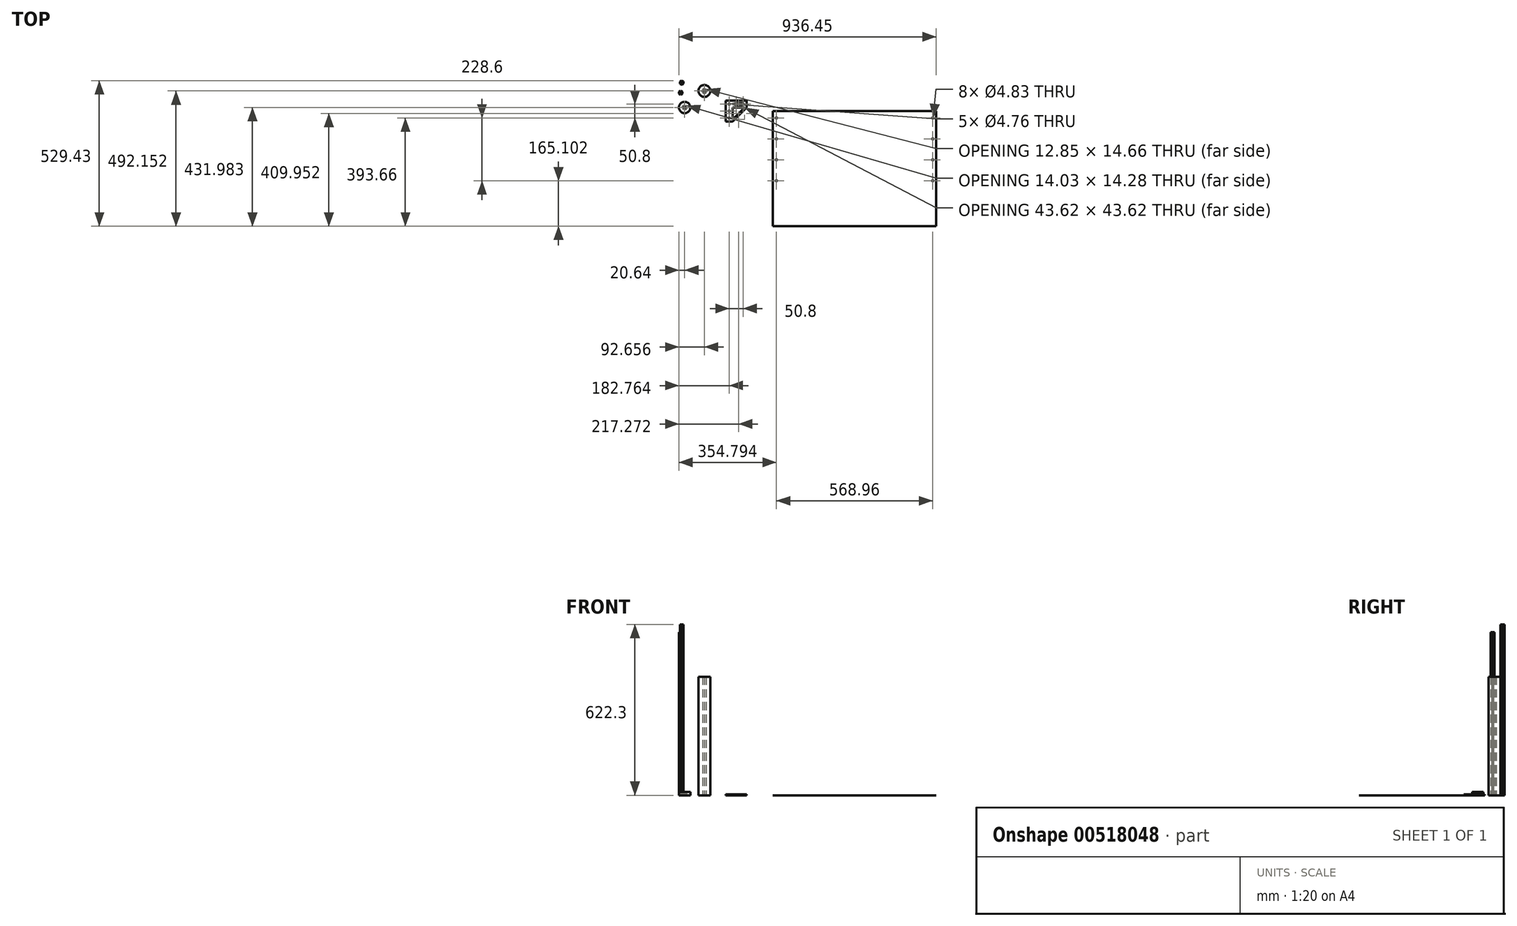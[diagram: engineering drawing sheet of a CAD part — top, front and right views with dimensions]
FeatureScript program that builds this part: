
annotation { "Feature Type Name" : "Feature", "Feature Type Description" : "" }
export const myFeature = defineFeature(function(context is Context, id is Id, definition is map)
    precondition{}
    {
        {
            var Q0;
            Q0=qCreatedBy(makeId("Top.planeOp"),FACE);
            var sketch = newSketch(context, id + "F0", { "sketchPlane" : qUnion([Q0])});
            skCircle(sketch, "E0.cCircle", {"center": v(-59.4, 64.97) * mm, "radius": 6.35 * mm, "construction": true});
            skLineSegment(sketch, "E0.0", {"start": v(-52.73, 61.92) * mm, "end": v(-58.7, 57.67) * mm});
            skLineSegment(sketch, "E0.1", {"start": v(-58.7, 57.67) * mm, "end": v(-65.37, 60.72) * mm});
            skLineSegment(sketch, "E0.2", {"start": v(-65.37, 60.72) * mm, "end": v(-66.07, 68.02) * mm});
            skLineSegment(sketch, "E0.3", {"start": v(-66.07, 68.02) * mm, "end": v(-60.1, 72.27) * mm});
            skLineSegment(sketch, "E0.4", {"start": v(-60.1, 72.27) * mm, "end": v(-53.42, 69.22) * mm});
            skLineSegment(sketch, "E0.5", {"start": v(-53.42, 69.22) * mm, "end": v(-52.73, 61.92) * mm});
            skPoint(sketch, "E0.0.midPoint", {"position": v(-55.71, 59.8) * mm});
            skCircle(sketch, "E1", {"center": v(-59.4, 64.97) * mm, "radius": 2.55 * mm});
            skSolve(sketch);
        }
        {
            var Q0;
            Q0=qSketchRegion(id+"F0",true);
            extrude(context, id + "F1", {"entities" : qUnion([Q0]), "depth" : 622.3 * mm});
        }
        {
            var Q0;
            Q0=qCreatedBy(makeId("Top.planeOp"),FACE);
            var sketch = newSketch(context, id + "F2", { "sketchPlane" : qUnion([Q0])});
            skCircle(sketch, "E2", {"center": v(23.03, 35) * mm, "radius": 21.59 * mm});
            skCircle(sketch, "E3.cCircle", {"center": v(23.03, 35) * mm, "radius": 6.35 * mm, "construction": true});
            skLineSegment(sketch, "E3.0", {"start": v(29.45, 31.46) * mm, "end": v(23.18, 27.66) * mm});
            skLineSegment(sketch, "E3.1", {"start": v(23.18, 27.66) * mm, "end": v(16.76, 31.2) * mm});
            skLineSegment(sketch, "E3.2", {"start": v(16.76, 31.2) * mm, "end": v(16.6, 38.52) * mm});
            skLineSegment(sketch, "E3.3", {"start": v(16.6, 38.52) * mm, "end": v(22.87, 42.32) * mm});
            skLineSegment(sketch, "E3.4", {"start": v(22.87, 42.32) * mm, "end": v(29.3, 38.8) * mm});
            skLineSegment(sketch, "E3.5", {"start": v(29.3, 38.8) * mm, "end": v(29.45, 31.46) * mm});
            skPoint(sketch, "E3.0.midPoint", {"position": v(26.32, 29.56) * mm});
            skSolve(sketch);
        }
        {
            var Q0;
            Q0=qSketchRegion(id+"F2",true);
            extrude(context, id + "F3", {"entities" : qUnion([Q0]), "depth" : 431.8 * mm});
        }
        {
            var Q0;
            Q0=qCreatedBy(makeId("Top.planeOp"),FACE);
            var sketch = newSketch(context, id + "F4", { "sketchPlane" : qUnion([Q0])});
            skLineSegment(sketch, "E4.bottom", {"start": v(272.46, -38.06) * mm, "end": v(866.82, -38.06) * mm});
            skLineSegment(sketch, "E4.top", {"start": v(272.46, -457.16) * mm, "end": v(866.82, -457.16) * mm});
            skLineSegment(sketch, "E4.left", {"start": v(272.46, -38.06) * mm, "end": v(272.46, -457.16) * mm});
            skLineSegment(sketch, "E4.right", {"start": v(866.82, -38.06) * mm, "end": v(866.82, -457.16) * mm});
            skPoint(sketch, "E4.middle", {"position": v(569.64, -247.6) * mm});
            skLineSegment(sketch, "E5", {"start": v(569.64, -38.06) * mm, "end": v(569.64, -457.16) * mm, "construction": true});
            skLineSegment(sketch, "E6", {"start": v(285.16, -38.06) * mm, "end": v(285.16, -457.16) * mm, "construction": true});
            skCircle(sketch, "E7", {"center": v(285.16, -63.46) * mm, "radius": 2.41 * mm});
            skCircle(sketch, "E8.0.1.0", {"center": v(285.16, -139.66) * mm, "radius": 2.41 * mm});
            skCircle(sketch, "E8.0.2.0", {"center": v(285.16, -215.86) * mm, "radius": 2.41 * mm});
            skCircle(sketch, "E8.0.3.0", {"center": v(285.16, -292.06) * mm, "radius": 2.41 * mm});
            skLineSegment(sketch, "E8.direction1", {"start": v(285.16, -63.46) * mm, "end": v(310.56, -63.46) * mm, "construction": true});
            skLineSegment(sketch, "E8.direction2", {"start": v(285.16, -63.46) * mm, "end": v(285.16, -139.66) * mm, "construction": true});
            skCircle(sketch, "E9.MirrorC", {"center": v(854.12, -292.06) * mm, "radius": 2.41 * mm});
            skCircle(sketch, "E10.MirrorC", {"center": v(854.12, -215.86) * mm, "radius": 2.41 * mm});
            skCircle(sketch, "E11.MirrorC", {"center": v(854.12, -139.66) * mm, "radius": 2.41 * mm});
            skCircle(sketch, "E12.MirrorC", {"center": v(854.12, -63.46) * mm, "radius": 2.41 * mm});
            skSolve(sketch);
        }
        {
            var Q0;
            Q0=makeQuery(id+"F4.imprint","IMPRINT",FACE,{"disambiguationData":[TD([[makeQuery(id+"F4.imprint","IMPRINT",EDGE,{"derivedFrom":sQuery(id+"F4.wireOp",EDGE,"E4.bottom")}),-1.0]])]});
            extrude(context, id + "F5", {"entities" : qUnion([Q0]), "depth" : 1 / 203.2 * mm});
        }
        {
            var Q0;
            Q0=qCreatedBy(makeId("Top.planeOp"),FACE);
            var sketch = newSketch(context, id + "F6", { "sketchPlane" : qUnion([Q0])});
            skCircle(sketch, "E13", {"center": v(-63.2, 28.56) * mm, "radius": 2.55 * mm});
            skCircle(sketch, "E14.cCircle", {"center": v(-63.2, 28.56) * mm, "radius": 6.35 * mm, "construction": true});
            skLineSegment(sketch, "E14.0", {"start": v(-56.85, 24.88) * mm, "end": v(-63.2, 21.22) * mm});
            skLineSegment(sketch, "E14.1", {"start": v(-63.2, 21.22) * mm, "end": v(-69.55, 24.9) * mm});
            skLineSegment(sketch, "E14.2", {"start": v(-69.55, 24.9) * mm, "end": v(-69.54, 32.23) * mm});
            skLineSegment(sketch, "E14.3", {"start": v(-69.54, 32.23) * mm, "end": v(-63.18, 35.89) * mm});
            skLineSegment(sketch, "E14.4", {"start": v(-63.18, 35.89) * mm, "end": v(-56.84, 32.21) * mm});
            skLineSegment(sketch, "E14.5", {"start": v(-56.84, 32.21) * mm, "end": v(-56.85, 24.88) * mm});
            skPoint(sketch, "E14.0.midPoint", {"position": v(-60.03, 23.05) * mm});
            skSolve(sketch);
        }
        {
            var Q0;
            Q0=makeQuery(id+"F6.imprint","IMPRINT",FACE,{"disambiguationData":[TD([[makeQuery(id+"F6.imprint","IMPRINT",EDGE,{"derivedFrom":sQuery(id+"F6.wireOp",EDGE,"E13")}),-1.0]])]});
            extrude(context, id + "F7", {"entities" : qUnion([Q0]), "depth" : 594.36 * mm});
        }
        {
            var Q0;
            Q0=qCreatedBy(makeId("Top.planeOp"),FACE);
            var sketch = newSketch(context, id + "F8", { "sketchPlane" : qUnion([Q0])});
            skCircle(sketch, "E15", {"center": v(-49, -25.18) * mm, "radius": 20.64 * mm});
            skCircle(sketch, "E16.cCircle", {"center": v(-49, -25.18) * mm, "radius": 6.35 * mm, "construction": true});
            skLineSegment(sketch, "E16.0", {"start": v(-43.64, -30.2) * mm, "end": v(-50.66, -32.32) * mm});
            skLineSegment(sketch, "E16.1", {"start": v(-50.66, -32.32) * mm, "end": v(-56, -27.3) * mm});
            skLineSegment(sketch, "E16.2", {"start": v(-56, -27.3) * mm, "end": v(-54.34, -20.16) * mm});
            skLineSegment(sketch, "E16.3", {"start": v(-54.34, -20.16) * mm, "end": v(-47.32, -18.04) * mm});
            skLineSegment(sketch, "E16.4", {"start": v(-47.32, -18.04) * mm, "end": v(-41.97, -23.05) * mm});
            skLineSegment(sketch, "E16.5", {"start": v(-41.97, -23.05) * mm, "end": v(-43.64, -30.2) * mm});
            skPoint(sketch, "E16.0.midPoint", {"position": v(-47.15, -31.25) * mm});
            skSolve(sketch);
        }
        {
            var Q0;
            Q0=makeQuery(id+"F8.imprint","IMPRINT",FACE,{"disambiguationData":[TD([[makeQuery(id+"F8.imprint","IMPRINT",EDGE,{"derivedFrom":sQuery(id+"F8.wireOp",EDGE,"E15")}),1.0]])]});
            extrude(context, id + "F9", {"entities" : qUnion([Q0]), "depth" : 12.7 * mm});
        }
        {
            var Q0;
            Q0=qCreatedBy(makeId("Top.planeOp"),FACE);
            var sketch = newSketch(context, id + "F10", { "sketchPlane" : qUnion([Q0])});
            skLineSegment(sketch, "E17", {"start": v(100.43, -76.2) * mm, "end": v(100.43, 0) * mm});
            skLineSegment(sketch, "E18", {"start": v(100.43, 0) * mm, "end": v(176.63, 0) * mm});
            skLineSegment(sketch, "E19", {"start": v(176.63, 0) * mm, "end": v(176.63, -25.4) * mm});
            skLineSegment(sketch, "E20", {"start": v(169.45, -25.4) * mm, "end": v(125.83, -25.4) * mm});
            skLineSegment(sketch, "E21", {"start": v(125.83, -25.4) * mm, "end": v(125.83, -69.02) * mm});
            skLineSegment(sketch, "E22", {"start": v(125.83, -76.2) * mm, "end": v(100.43, -76.2) * mm});
            skLineSegment(sketch, "E23", {"start": v(125.83, -76.2) * mm, "end": v(176.63, -25.4) * mm});
            skLineSegment(sketch, "E24", {"start": v(169.45, -25.4) * mm, "end": v(125.83, -69.02) * mm});
            skCircle(sketch, "E25", {"center": v(113.13, -63.5) * mm, "radius": 2.38 * mm});
            skPoint(sketch, "E25.centerSnap0", {"position": v(113.13, -76.2) * mm});
            skCircle(sketch, "E26", {"center": v(113.13, -38.1) * mm, "radius": 2.38 * mm});
            skCircle(sketch, "E27", {"center": v(113.13, -12.7) * mm, "radius": 2.38 * mm});
            skCircle(sketch, "E28", {"center": v(138.53, -12.7) * mm, "radius": 2.38 * mm});
            skCircle(sketch, "E29", {"center": v(163.93, -12.7) * mm, "radius": 2.38 * mm});
            skLineSegment(sketch, "E30", {"start": v(163.93, -12.7) * mm, "end": v(113.13, -12.7) * mm, "construction": true});
            skLineSegment(sketch, "E31", {"start": v(113.13, -12.7) * mm, "end": v(113.13, -63.5) * mm, "construction": true});
            skPoint(sketch, "E32", {"position": v(100.43, -38.1) * mm});
            skPoint(sketch, "E33", {"position": v(138.53, 0) * mm});
            skSolve(sketch);
        }
        {
            var Q0;
            Q0=qSketchRegion(id+"F10",true);
            extrude(context, id + "F11", {"entities" : qUnion([Q0]), "depth" : 3.17 * mm});
        }
    });
